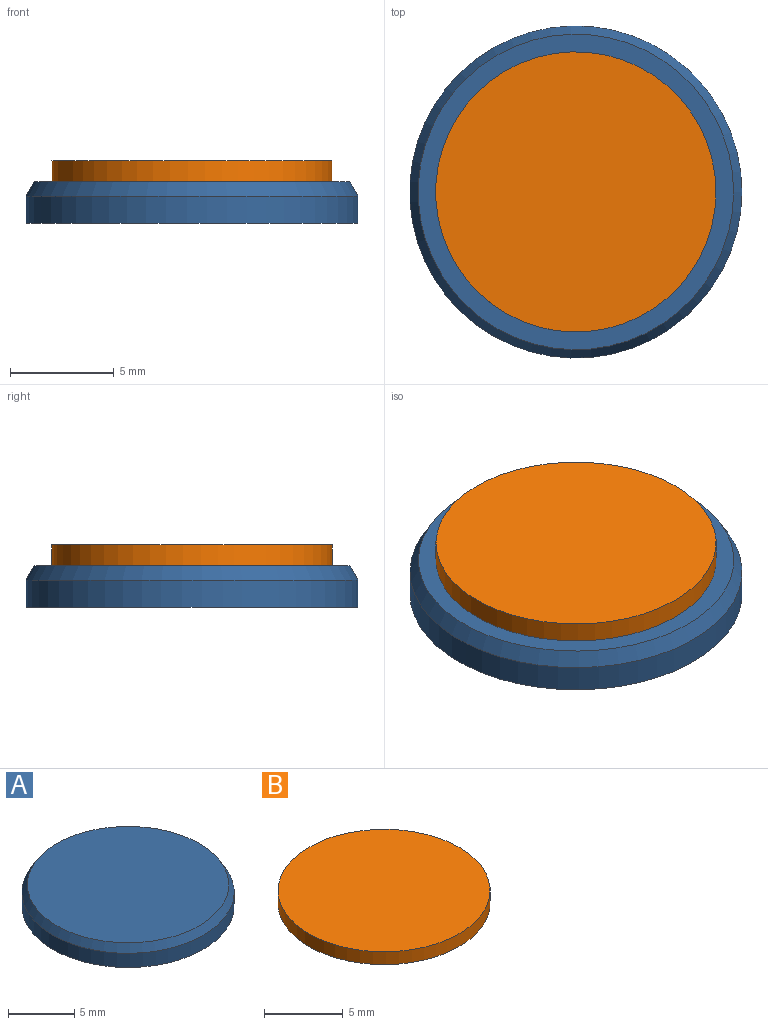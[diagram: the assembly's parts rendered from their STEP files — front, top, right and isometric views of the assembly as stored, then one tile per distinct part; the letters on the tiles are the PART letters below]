
ASSEMBLY  parts=2 mates=1
PART A: 4 faces, bbox 16x16x2 mm
  f0: cylinder r=8mm len=16mm, axis (0,0,-1), area 65.7mm2, adj f2,f3
  f1: plane 15.2x15.2mm, normal (0,0,1), area 181.5mm2, adj f3
  f2: plane 16x16mm, normal (0,0,-1), area 201.1mm2, adj f0
  f3: cone r=7.6mm half-angle=30deg, axis (0,0,-1), area 39.2mm2, adj f0,f1
PART B: 3 faces, bbox 13.5x13.5x1 mm
  f0: cylinder r=6.75mm len=13.5mm, axis (0,0,-1), area 42.4mm2, adj f1,f2
  f1: plane 13.5x13.5mm, normal (0,0,1), area 143.1mm2, adj f0
  f2: plane 13.5x13.5mm, normal (0,0,-1), area 143.1mm2, adj f0
PLACE A t=(-3.12,-0.05,0.43)mm
PLACE B t=(-3.12,-0.05,2.43)mm
MATE fastened A.f0 <-> B.f0  axis (0,0,1) through (-3.12,-0.05,2.43)mm
